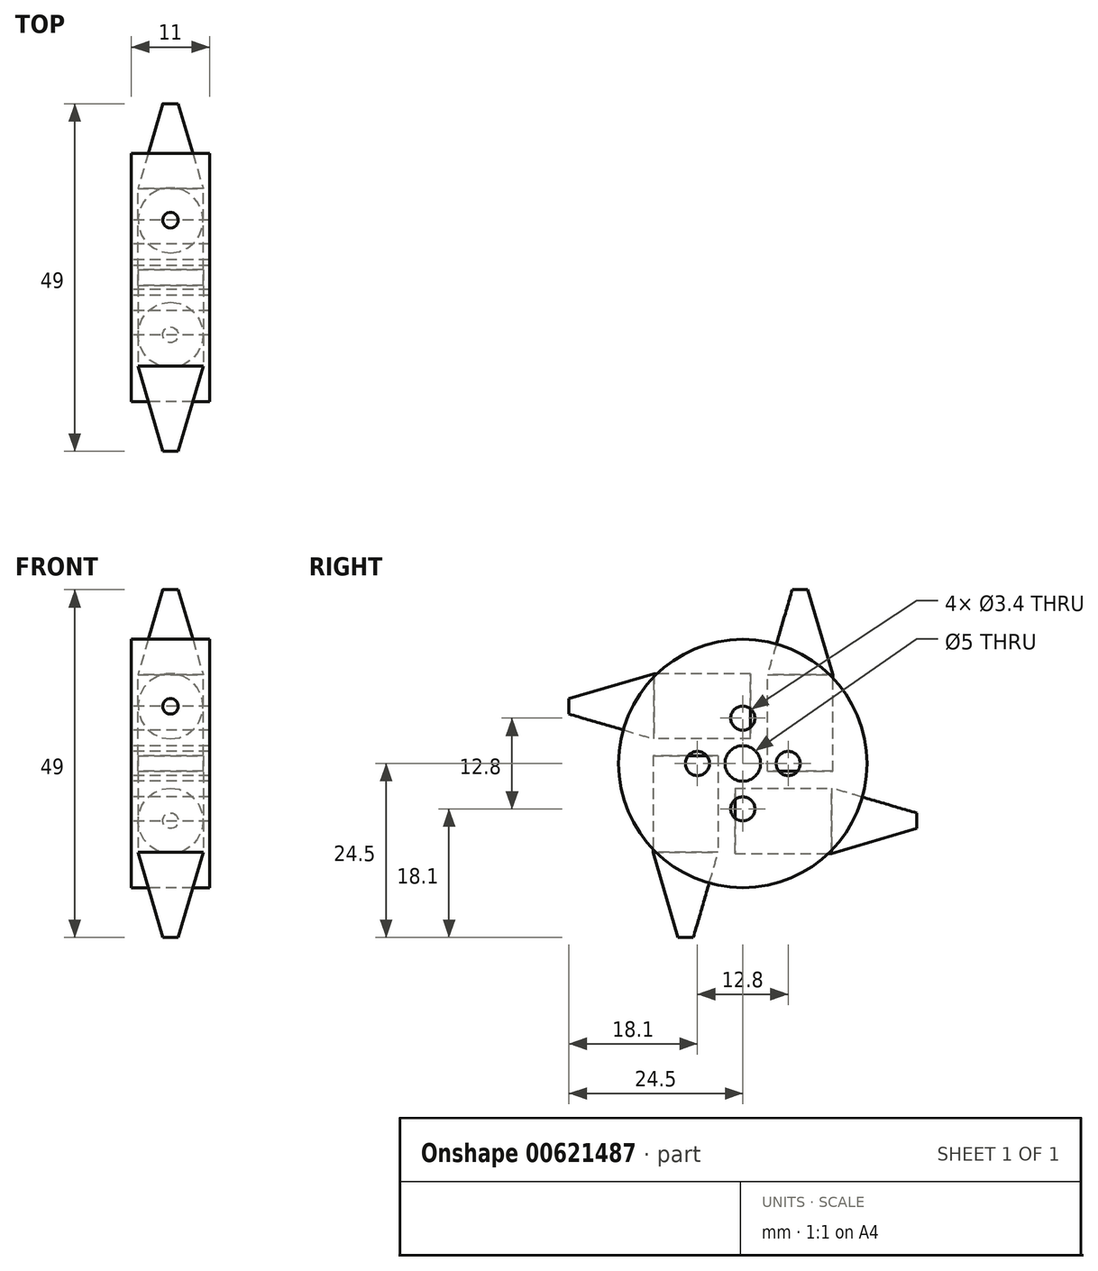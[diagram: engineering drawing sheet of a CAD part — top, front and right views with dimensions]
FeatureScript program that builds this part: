
annotation { "Feature Type Name" : "Feature", "Feature Type Description" : "" }
export const myFeature = defineFeature(function(context is Context, id is Id, definition is map)
    precondition{}
    {
        {
            var Q0;
            Q0=qCreatedBy(makeId("Right.planeOp"),FACE);
            var sketch = newSketch(context, id + "F0", { "sketchPlane" : qUnion([Q0])});
            skCircle(sketch, "E0", {"center": v(0, 0) * mm, "radius": 17.5 * mm});
            skCircle(sketch, "E1", {"center": v(0, 0) * mm, "radius": 2.5 * mm});
            skCircle(sketch, "E2", {"center": v(0, 6.4) * mm, "radius": 1.7 * mm});
            skCircle(sketch, "E3", {"center": v(6.4, 0) * mm, "radius": 1.7 * mm});
            skCircle(sketch, "E4", {"center": v(0, -6.4) * mm, "radius": 1.7 * mm});
            skCircle(sketch, "E5", {"center": v(-6.4, 0) * mm, "radius": 1.7 * mm});
            skSolve(sketch);
        }
        {
            var Q0;
            Q0 = qSketchRegion(id + "F0", true);
            extrude(context, id + "F1", {"entities" : qUnion([Q0]), "depth" : 11 * mm, "offsetDistance" : 25 * mm, "symmetric" : true});
        }
        {
            var Q0;
            Q0=qCreatedBy(makeId("Top.planeOp"),FACE);
            var sketch = newSketch(context, id + "F2", { "sketchPlane" : qUnion([Q0])});
            skLineSegment(sketch, "E6", {"start": v(-19.71, 0) * mm, "end": v(30.41, 0) * mm});
            skSolve(sketch);
        }
        {
            var Q0;
            Q0=qCreatedBy(makeId("Right.planeOp"),FACE);
            var sketch = newSketch(context, id + "F3", { "sketchPlane" : qUnion([Q0])});
            skLineSegment(sketch, "E7.top", {"start": v(1.1, 8.07) * mm, "end": v(1.1, 3.47) * mm});
            skLineSegment(sketch, "E7.left", {"start": v(-12.5, 8.07) * mm, "end": v(1.1, 8.07) * mm});
            skLineSegment(sketch, "E7.right", {"start": v(-12.5, 3.47) * mm, "end": v(1.1, 3.47) * mm});
            skLineSegment(sketch, "E8", {"start": v(-12.5, 3.47) * mm, "end": v(-24.5, 6.97) * mm});
            skLineSegment(sketch, "E9", {"start": v(-24.5, 6.97) * mm, "end": v(-24.5, 8.07) * mm});
            skLineSegment(sketch, "E10", {"start": v(-24.5, 8.07) * mm, "end": v(-12.5, 8.07) * mm});
            skSolve(sketch);
        }
        {
            var Q0;
            Q0=makeQuery(id+"F3.imprint","IMPRINT",FACE,{"disambiguationData":[TD([[makeQuery(id+"F3.imprint","IMPRINT",EDGE,{"derivedFrom":sQuery(id+"F3.wireOp",EDGE,"E7.top")}),-1.0]])]});
            var Q1;
            Q1=sQuery(id+"F3.wireOp",EDGE,"E10");
            revolve(context, id + "F4", {"entities" : qUnion([Q0]), "axis" : qUnion([Q1]), "revolveType" : RevolveType.FULL});
        }
        {
            var Q0;
            Q0=makeQuery(id+"F4.opRevolve","SWEPT_BODY",BODY,{"disambiguationData":[OSD([sQuery(id+"F3.wireOp",EDGE,"E7.top"),sQuery(id+"F3.wireOp",EDGE,"E7.left"),sQuery(id+"F3.wireOp",EDGE,"E7.right"),sQuery(id+"F3.wireOp",EDGE,"E8"),sQuery(id+"F3.wireOp",EDGE,"E9"),sQuery(id+"F3.wireOp",EDGE,"E10")])]});
            var Q1;
            Q1=sQuery(id+"F2.wireOp",EDGE,"E6");
            circularPattern(context, id + "F5", {"entities" : qUnion([Q0]), "axis" : qUnion([Q1]), "angle" : 360 * degree, "instanceCount" : 4, "equalSpace" : true});
        }
    });
